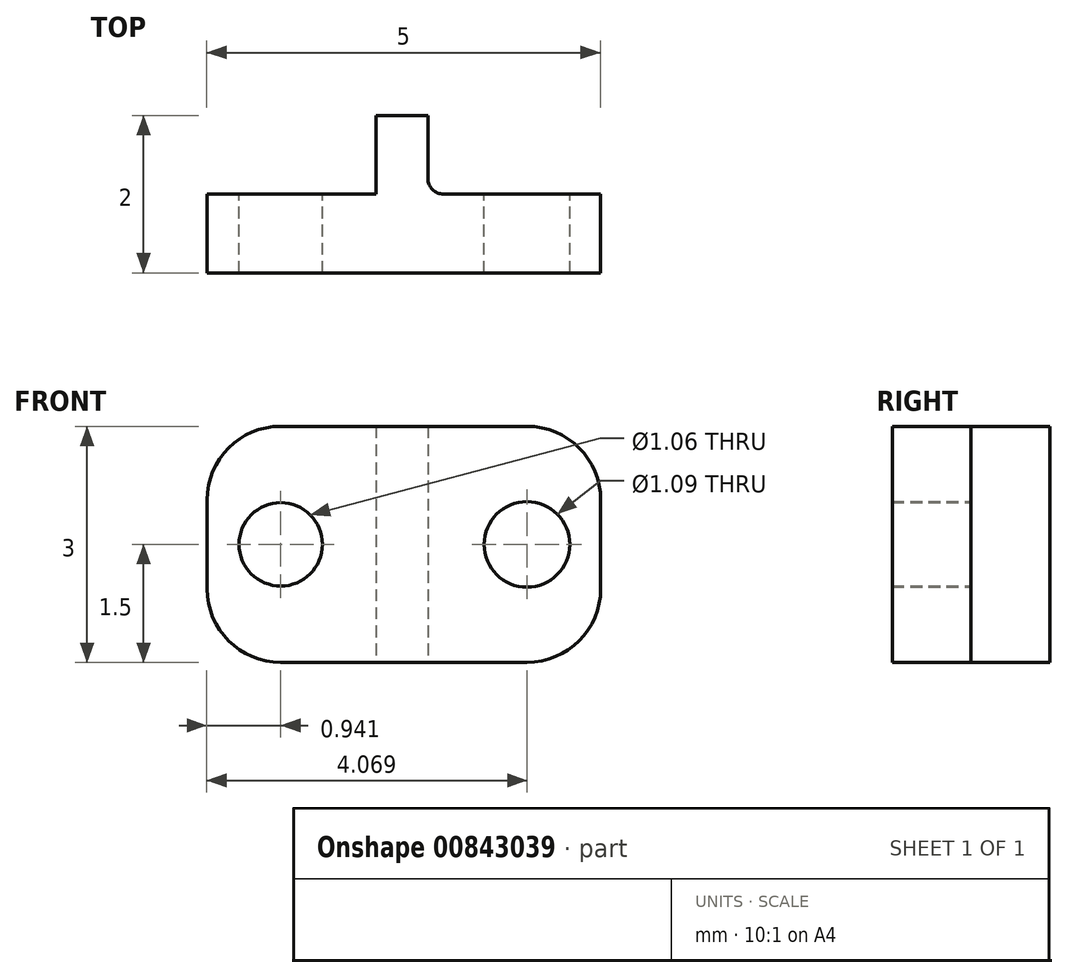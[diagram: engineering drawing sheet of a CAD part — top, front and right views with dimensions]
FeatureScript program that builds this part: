
annotation { "Feature Type Name" : "Feature", "Feature Type Description" : "" }
export const myFeature = defineFeature(function(context is Context, id is Id, definition is map)
    precondition{}
    {
        {
            var Q0;
            Q0=qCreatedBy(makeId("Front.planeOp"),FACE);
            var sketch = newSketch(context, id + "F0", { "sketchPlane" : qUnion([Q0])});
            skLineSegment(sketch, "E0.bottom", {"start": v(2.97, -0.96) * mm, "end": v(6.1, -0.96) * mm});
            skLineSegment(sketch, "E0.top", {"start": v(2.97, -3.96) * mm, "end": v(6.1, -3.96) * mm});
            skLineSegment(sketch, "E0.left", {"start": v(2.03, -1.9) * mm, "end": v(2.03, -3.02) * mm});
            skLineSegment(sketch, "E0.right", {"start": v(7.03, -1.9) * mm, "end": v(7.03, -3.02) * mm});
            skPoint(sketch, "E1.visualSharp", {"position": v(2.03, -0.96) * mm});
            skArc(sketch, "E1.filletArc", {"start": v(2.97, -0.96) * mm, "mid": v(2.3, -1.23) * mm, "end": v(2.03, -1.9) * mm});
            skPoint(sketch, "E2.visualSharp", {"position": v(2.03, -3.96) * mm});
            skArc(sketch, "E2.filletArc", {"start": v(2.03, -3.02) * mm, "mid": v(2.3, -3.69) * mm, "end": v(2.97, -3.96) * mm});
            skPoint(sketch, "E3.visualSharp", {"position": v(7.03, -3.96) * mm});
            skArc(sketch, "E3.filletArc", {"start": v(6.1, -3.96) * mm, "mid": v(6.76, -3.69) * mm, "end": v(7.03, -3.02) * mm});
            skPoint(sketch, "E4.visualSharp", {"position": v(7.03, -0.96) * mm});
            skArc(sketch, "E4.filletArc", {"start": v(7.03, -1.9) * mm, "mid": v(6.76, -1.23) * mm, "end": v(6.1, -0.96) * mm});
            skCircle(sketch, "E5", {"center": v(2.97, -2.46) * mm, "radius": 0.53 * mm});
            skPoint(sketch, "E5.centerSnap0", {"position": v(2.03, -2.46) * mm});
            skCircle(sketch, "E6", {"center": v(6.1, -2.46) * mm, "radius": 0.54 * mm});
            skPoint(sketch, "E6.centerSnap0", {"position": v(7.03, -2.46) * mm});
            skSolve(sketch);
        }
        {
            var Q0;
            Q0=makeQuery(id+"F0.imprint","IMPRINT",FACE,{"disambiguationData":[TD([[makeQuery(id+"F0.imprint","IMPRINT",EDGE,{"derivedFrom":sQuery(id+"F0.wireOp",EDGE,"E0.bottom")}),-1.0]])]});
            extrude(context, id + "F1", {"entities" : qUnion([Q0]), "depth" : 1 * mm, "offsetDistance" : 25 * mm});
        }
        {
            var Q0;
            Q0=makeQuery(id+"F1.opExtrude","CAP_FACE",FACE,{"disambiguationData":[OSD([sQuery(id+"F0.wireOp",EDGE,"E0.bottom"),sQuery(id+"F0.wireOp",EDGE,"E0.top"),sQuery(id+"F0.wireOp",EDGE,"E0.left"),sQuery(id+"F0.wireOp",EDGE,"E0.right"),sQuery(id+"F0.wireOp",EDGE,"E1.filletArc"),sQuery(id+"F0.wireOp",EDGE,"E2.filletArc"),sQuery(id+"F0.wireOp",EDGE,"E3.filletArc"),sQuery(id+"F0.wireOp",EDGE,"E4.filletArc"),sQuery(id+"F0.wireOp",EDGE,"E5"),sQuery(id+"F0.wireOp",EDGE,"E6")])],"isStart":true});
            var sketch = newSketch(context, id + "F2", { "sketchPlane" : qUnion([Q0])});
            skLineSegment(sketch, "E7.bottom", {"start": v(-4.84, -0.96) * mm, "end": v(-4.18, -0.96) * mm});
            skLineSegment(sketch, "E7.top", {"start": v(-4.84, -3.96) * mm, "end": v(-4.18, -3.96) * mm});
            skLineSegment(sketch, "E7.left", {"start": v(-4.84, -0.96) * mm, "end": v(-4.84, -3.96) * mm});
            skLineSegment(sketch, "E7.right", {"start": v(-4.18, -0.96) * mm, "end": v(-4.18, -3.96) * mm});
            skSolve(sketch);
        }
        {
            var Q0;
            Q0=makeQuery(id+"F2.imprint","IMPRINT",FACE,{"disambiguationData":[TD([[makeQuery(id+"F2.imprint","IMPRINT",EDGE,{"derivedFrom":sQuery(id+"F2.wireOp",EDGE,"E7.bottom")}),1.0]])]});
            extrude(context, id + "F3", {"entities" : qUnion([Q0]), "operationType" : NewBodyOperationType.ADD, "depth" : 1 * mm, "offsetDistance" : 25 * mm});
        }
        {
            var Q0;
            Q0=makeQuery(id+"F3.opExtrude","CAP_EDGE",EDGE,{"disambiguationData":[OSD([sQuery(id+"F2.wireOp",EDGE,"E7.left")])],"isStart":true});
            var Q1;
            Q1=makeQuery(id+"F3.opExtrude","CAP_EDGE",EDGE,{"disambiguationData":[OSD([sQuery(id+"F2.wireOp",EDGE,"E7.right")])],"isStart":true});
            fillet(context, id + "F4", {"entities" : qUnion([Q0, Q1]), "radius" : 0.2 * mm, "tangentPropagation" : true, "allowEdgeOverflow" : false});
        }
    });
